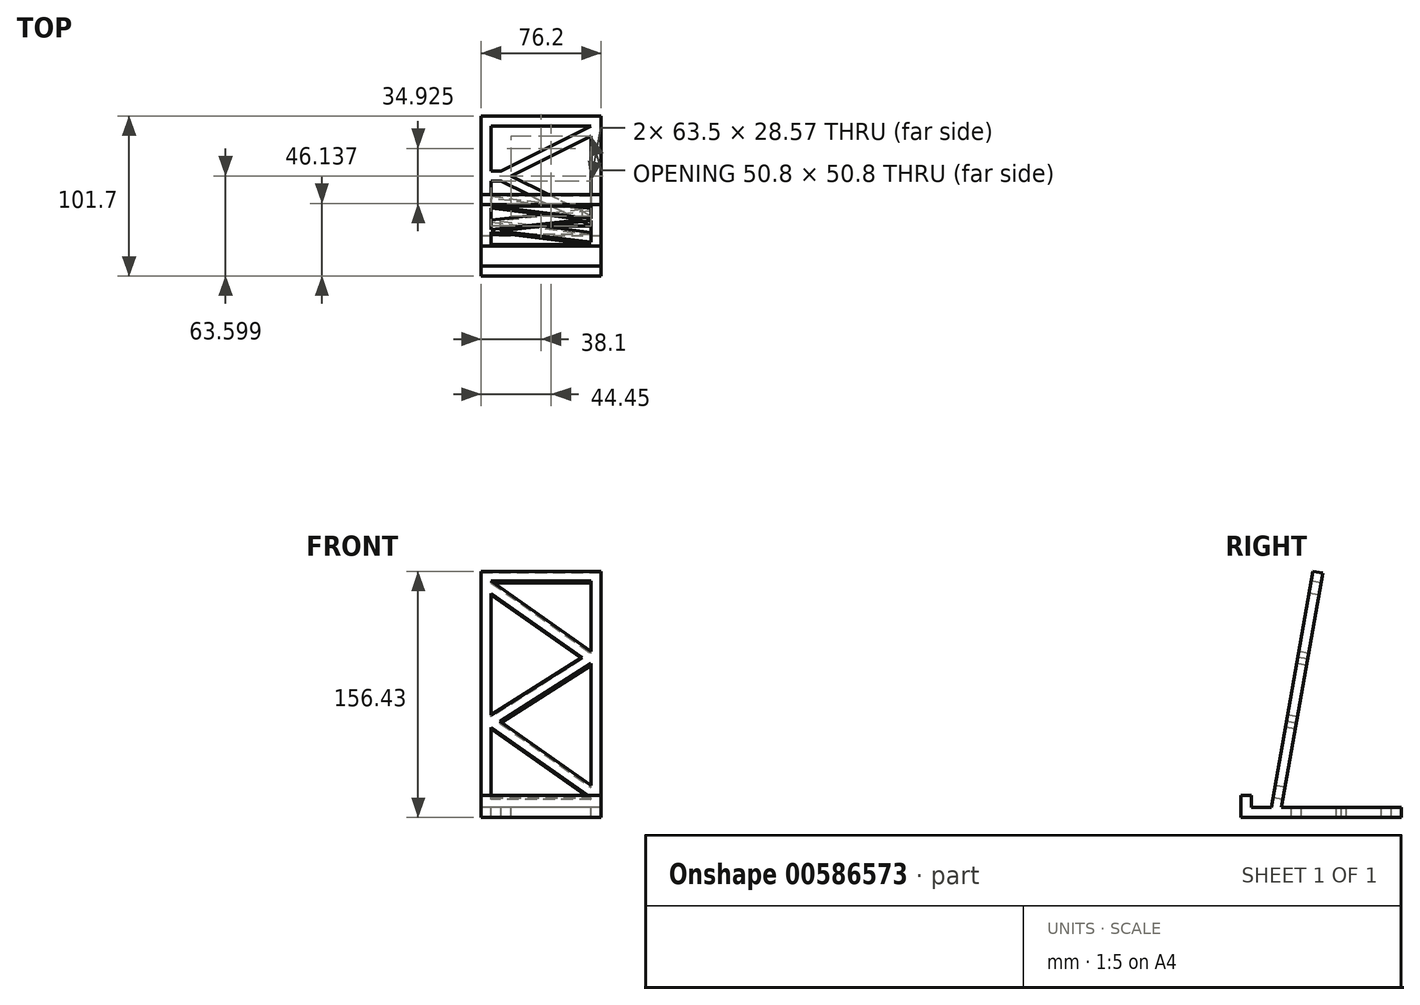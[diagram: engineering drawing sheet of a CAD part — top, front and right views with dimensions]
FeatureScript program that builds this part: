
annotation { "Feature Type Name" : "Feature", "Feature Type Description" : "" }
export const myFeature = defineFeature(function(context is Context, id is Id, definition is map)
    precondition{}
    {
        {
            var Q0;
            Q0=qCreatedBy(makeId("Right.planeOp"),FACE);
            var sketch = newSketch(context, id + "F0", { "sketchPlane" : qUnion([Q0])});
            skLineSegment(sketch, "E0", {"start": v(-44.45, 13.97) * mm, "end": v(-44.45, 0) * mm});
            skLineSegment(sketch, "E1", {"start": v(-44.45, 0) * mm, "end": v(57.25, 0) * mm});
            skLineSegment(sketch, "E2", {"start": v(57.25, 0) * mm, "end": v(57.25, 6.35) * mm});
            skLineSegment(sketch, "E3", {"start": v(57.25, 6.35) * mm, "end": v(-18.95, 6.35) * mm});
            skLineSegment(sketch, "E4", {"start": v(-18.95, 6.35) * mm, "end": v(7.32, 155.33) * mm});
            skLineSegment(sketch, "E5", {"start": v(7.32, 155.33) * mm, "end": v(1.07, 156.43) * mm});
            skLineSegment(sketch, "E6", {"start": v(1.07, 156.43) * mm, "end": v(-25.4, 6.35) * mm});
            skLineSegment(sketch, "E7", {"start": v(-25.4, 6.35) * mm, "end": v(-38.1, 6.35) * mm});
            skLineSegment(sketch, "E8", {"start": v(-38.1, 6.35) * mm, "end": v(-38.1, 13.97) * mm});
            skLineSegment(sketch, "E9", {"start": v(-38.1, 13.97) * mm, "end": v(-44.45, 13.97) * mm});
            skSolve(sketch);
        }
        {
            var Q0;
            Q0=makeQuery(id+"F0.imprint","IMPRINT",FACE,{"disambiguationData":[TD([[makeQuery(id+"F0.imprint","IMPRINT",EDGE,{"derivedFrom":sQuery(id+"F0.wireOp",EDGE,"E0")}),1.0]])]});
            extrude(context, id + "F1", {"entities" : qUnion([Q0]), "endBound" : BoundingType.SYMMETRIC, "depth" : 76.2 * mm, "offsetDistance" : 25.4 * mm});
        }
        {
            var Q0;
            Q0=makeQuery(id+"F1.opExtrude","SWEPT_FACE",FACE,{"disambiguationData":[OSD([sQuery(id+"F0.wireOp",EDGE,"E3")])]});
            var sketch = newSketch(context, id + "F2", { "sketchPlane" : qUnion([Q0])});
            skLineSegment(sketch, "E10.bottom", {"start": v(31.75, 50.9) * mm, "end": v(-31.75, 50.9) * mm});
            skLineSegment(sketch, "E10.top", {"start": v(31.75, -12.6) * mm, "end": v(-31.75, -12.6) * mm});
            skLineSegment(sketch, "E10.left", {"start": v(31.75, 50.9) * mm, "end": v(31.75, -12.6) * mm});
            skLineSegment(sketch, "E10.right", {"start": v(-31.75, 50.9) * mm, "end": v(-31.75, -12.6) * mm});
            skLineSegment(sketch, "E11", {"start": v(31.75, 50.9) * mm, "end": v(-31.75, 19.15) * mm});
            skLineSegment(sketch, "E12", {"start": v(-31.75, 19.15) * mm, "end": v(31.75, -12.6) * mm});
            skLineSegment(sketch, "E13", {"start": v(31.75, 44.55) * mm, "end": v(-25.4, 15.97) * mm});
            skLineSegment(sketch, "E14", {"start": v(31.75, -6.25) * mm, "end": v(-25.4, 22.32) * mm});
            skLineSegment(sketch, "E15", {"start": v(-25.4, 22.32) * mm, "end": v(-31.75, 22.32) * mm});
            skLineSegment(sketch, "E16", {"start": v(-25.4, 15.97) * mm, "end": v(-31.75, 15.97) * mm});
            skSolve(sketch);
        }
        {
            var Q0;
            {var subQ0=sQuery(id+"F2.wireOp",EDGE,"E10.top");Q0=makeQuery(id+"F2.imprint","IMPRINT",FACE,{"disambiguationData":[TD([[makeQuery(id+"F2.imprint","IMPRINT",EDGE,{"derivedFrom":subQ0}),-1.0]])]});}
            var Q1;
            {var subQ0=sQuery(id+"F2.wireOp",EDGE,"E13");var subQ1=sQuery(id+"F2.wireOp",EDGE,"E10.left");var subQ2=makeQuery(id+"F2.imprint","INTERSECT",VERTEX,{"derivedFrom":[subQ1,subQ0]});Q1=makeQuery(id+"F2.imprint","IMPRINT",FACE,{"disambiguationData":[TD([[makeQuery(id+"F2.imprint","IMPRINT",EDGE,{"disambiguationData":[TD([[subQ2,-1.0]])],"derivedFrom":subQ1}),-1.0]])]});}
            var Q2;
            {var subQ0=sQuery(id+"F2.wireOp",EDGE,"E10.bottom");Q2=makeQuery(id+"F2.imprint","IMPRINT",FACE,{"disambiguationData":[TD([[makeQuery(id+"F2.imprint","IMPRINT",EDGE,{"derivedFrom":subQ0}),1.0]])]});}
            extrude(context, id + "F3", {"entities" : qUnion([Q0, Q1, Q2]), "operationType" : NewBodyOperationType.REMOVE, "oppositeDirection" : true, "depth" : 25.4 * mm, "offsetDistance" : 25.4 * mm});
        }
        {
            var Q0;
            Q0=makeQuery(id+"F1.opExtrude","SWEPT_FACE",FACE,{"disambiguationData":[OSD([sQuery(id+"F0.wireOp",EDGE,"E6")])]});
            var sketch = newSketch(context, id + "F4", { "sketchPlane" : qUnion([Q0])});
            skLineSegment(sketch, "E17.bottom", {"start": v(-31.75, 147.9) * mm, "end": v(31.75, 147.9) * mm});
            skLineSegment(sketch, "E17.top", {"start": v(-31.75, 8.2) * mm, "end": v(31.75, 8.2) * mm});
            skLineSegment(sketch, "E17.left", {"start": v(-31.75, 147.9) * mm, "end": v(-31.75, 8.2) * mm});
            skLineSegment(sketch, "E17.right", {"start": v(31.75, 147.9) * mm, "end": v(31.75, 8.2) * mm});
            skLineSegment(sketch, "E18", {"start": v(31.75, 8.2) * mm, "end": v(-31.75, 53.62) * mm});
            skLineSegment(sketch, "E19", {"start": v(31.75, 16) * mm, "end": v(-31.75, 61.43) * mm});
            skLineSegment(sketch, "E20", {"start": v(-31.75, 53.62) * mm, "end": v(31.75, 94.66) * mm});
            skLineSegment(sketch, "E21", {"start": v(-31.75, 61.43) * mm, "end": v(31.75, 102.47) * mm});
            skLineSegment(sketch, "E22", {"start": v(31.75, 102.47) * mm, "end": v(-31.75, 147.9) * mm});
            skLineSegment(sketch, "E23", {"start": v(-31.75, 140.09) * mm, "end": v(31.75, 94.66) * mm});
            skSolve(sketch);
        }
        {
            var Q0;
            {var subQ0=sQuery(id+"F4.wireOp",EDGE,"E17.bottom");Q0=makeQuery(id+"F4.imprint","IMPRINT",FACE,{"disambiguationData":[TD([[makeQuery(id+"F4.imprint","IMPRINT",EDGE,{"derivedFrom":subQ0}),-1.0]])]});}
            var Q1;
            {var subQ1=sQuery(id+"F4.wireOp",EDGE,"E17.left");var subQ3=sQuery(id+"F4.wireOp",EDGE,"E23");var subQ4=makeQuery(id+"F4.imprint","INTERSECT",VERTEX,{"derivedFrom":[subQ1,subQ3]});Q1=makeQuery(id+"F4.imprint","IMPRINT",FACE,{"disambiguationData":[TD([[makeQuery(id+"F4.imprint","IMPRINT",EDGE,{"disambiguationData":[TD([[subQ4,-1.0]])],"derivedFrom":subQ3}),-1.0]])]});}
            var Q2;
            {var subQ0=sQuery(id+"F4.wireOp",EDGE,"E19");var subQ1=sQuery(id+"F4.wireOp",EDGE,"E17.right");var subQ2=makeQuery(id+"F4.imprint","INTERSECT",VERTEX,{"derivedFrom":[subQ1,subQ0]});Q2=makeQuery(id+"F4.imprint","IMPRINT",FACE,{"disambiguationData":[TD([[makeQuery(id+"F4.imprint","IMPRINT",EDGE,{"disambiguationData":[TD([[subQ2,-1.0]])],"derivedFrom":subQ0}),-1.0]])]});}
            var Q3;
            {var subQ0=sQuery(id+"F4.wireOp",EDGE,"E17.top");Q3=makeQuery(id+"F4.imprint","IMPRINT",FACE,{"disambiguationData":[TD([[makeQuery(id+"F4.imprint","IMPRINT",EDGE,{"derivedFrom":subQ0}),1.0]])]});}
            var Q4;
            Q4=makeQuery(id+"F1.opExtrude","SWEPT_FACE",FACE,{"disambiguationData":[OSD([sQuery(id+"F0.wireOp",EDGE,"E4")])]});
            extrude(context, id + "F5", {"entities" : qUnion([Q0, Q1, Q2, Q3]), "operationType" : NewBodyOperationType.REMOVE, "endBound" : BoundingType.UP_TO_SURFACE, "oppositeDirection" : true, "depth" : 25.4 * mm, "endBoundEntityFace" : qUnion([Q4]), "offsetDistance" : 25.4 * mm});
        }
    });
